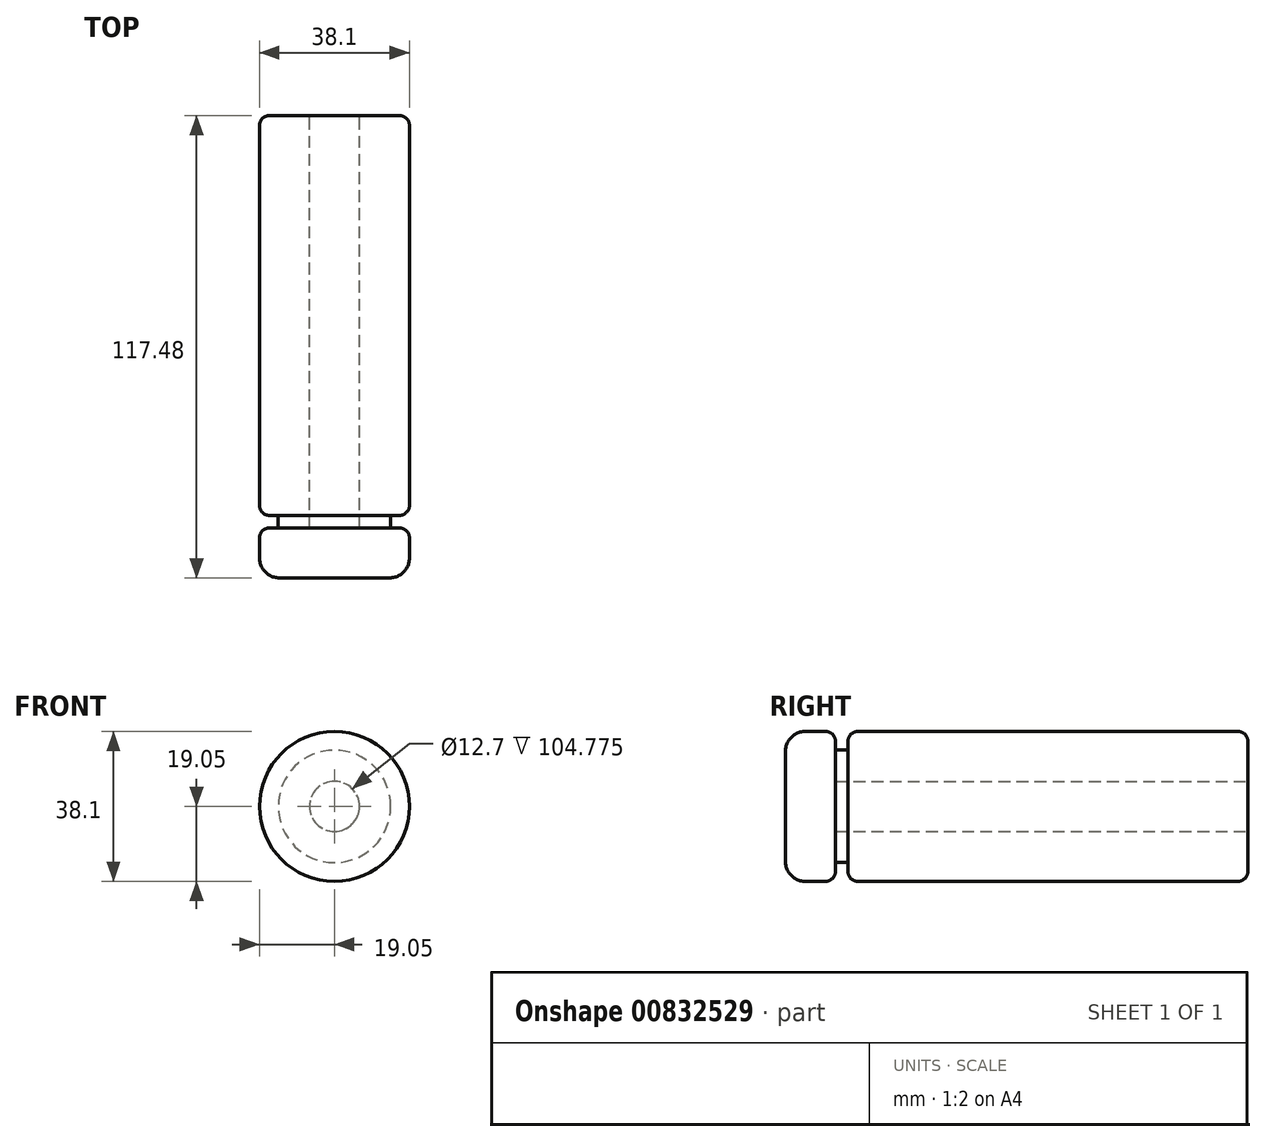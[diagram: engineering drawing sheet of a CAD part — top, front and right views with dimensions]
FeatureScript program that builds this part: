
annotation { "Feature Type Name" : "Feature", "Feature Type Description" : "" }
export const myFeature = defineFeature(function(context is Context, id is Id, definition is map)
    precondition{}
    {
        {
            var Q0;
            Q0=qCreatedBy(makeId("Front.planeOp"),FACE);
            var sketch = newSketch(context, id + "F0", { "sketchPlane" : qUnion([Q0])});
            skCircle(sketch, "E0", {"center": v(0, 0) * mm, "radius": 19.05 * mm});
            skSolve(sketch);
        }
        {
            var Q0;
            Q0=makeQuery(id+"F0.imprint","IMPRINT",FACE,{"disambiguationData":[TD([[makeQuery(id+"F0.imprint","IMPRINT",EDGE,{"derivedFrom":sQuery(id+"F0.wireOp",EDGE,"E0")}),1.0]])]});
            extrude(context, id + "F1", {"entities" : qUnion([Q0]), "depth" : 101.6 * mm, "offsetDistance" : 25.4 * mm});
        }
        {
            var Q0;
            Q0=makeQuery(id+"F1.opExtrude","CAP_EDGE",EDGE,{"disambiguationData":[OSD([sQuery(id+"F0.wireOp",EDGE,"E0")])],"isStart":false});
            var Q1;
            Q1=makeQuery(id+"F1.opExtrude","CAP_EDGE",EDGE,{"disambiguationData":[OSD([sQuery(id+"F0.wireOp",EDGE,"E0")])],"isStart":true});
            fillet(context, id + "F2", {"entities" : qUnion([Q0, Q1]), "radius" : 2.54 * mm, "tangentPropagation" : true, "allowEdgeOverflow" : false});
        }
        {
            var Q0;
            Q0=makeQuery(id+"F1.opExtrude","CAP_FACE",FACE,{"disambiguationData":[OSD([sQuery(id+"F0.wireOp",EDGE,"E0")])],"isStart":true});
            var sketch = newSketch(context, id + "F3", { "sketchPlane" : qUnion([Q0])});
            skCircle(sketch, "E1", {"center": v(0, 0) * mm, "radius": 6.35 * mm});
            skSolve(sketch);
        }
        {
            var Q0;
            Q0=makeQuery(id+"F1.opExtrude","CAP_FACE",FACE,{"disambiguationData":[OSD([sQuery(id+"F0.wireOp",EDGE,"E0")])],"isStart":false});
            var sketch = newSketch(context, id + "F4", { "sketchPlane" : qUnion([Q0])});
            skCircle(sketch, "E2", {"center": v(0, 0) * mm, "radius": 6.35 * mm});
            skSolve(sketch);
        }
        {
            var Q0;
            Q0=makeQuery(id+"F4.imprint","IMPRINT",FACE,{"disambiguationData":[TD([[makeQuery(id+"F4.imprint","IMPRINT",EDGE,{"derivedFrom":sQuery(id+"F4.wireOp",EDGE,"E2")}),1.0]])]});
            var sketch = newSketch(context, id + "F5", { "sketchPlane" : qUnion([Q0])});
            skCircle(sketch, "E3", {"center": v(0, 0) * mm, "radius": 6.35 * mm});
            skCircle(sketch, "E4", {"center": v(0, 0) * mm, "radius": 14.29 * mm});
            skSolve(sketch);
        }
        {
            var Q0;
            Q0=makeQuery(id+"F5.imprint","IMPRINT",FACE,{"disambiguationData":[TD([[makeQuery(id+"F5.imprint","IMPRINT",EDGE,{"derivedFrom":sQuery(id+"F5.wireOp",EDGE,"E3")}),-1.0]])]});
            extrude(context, id + "F6", {"entities" : qUnion([Q0]), "operationType" : NewBodyOperationType.ADD, "depth" : 3.17 * mm, "offsetDistance" : 25.4 * mm});
        }
        {
            var Q0;
            Q0=makeQuery(id+"F6.opExtrude","CAP_FACE",FACE,{"disambiguationData":[OSD([sQuery(id+"F5.wireOp",EDGE,"E3"),sQuery(id+"F5.wireOp",EDGE,"E4")])],"isStart":false});
            var sketch = newSketch(context, id + "F7", { "sketchPlane" : qUnion([Q0])});
            skCircle(sketch, "E5", {"center": v(0, 0) * mm, "radius": 19.05 * mm});
            skSolve(sketch);
        }
        {
            var Q0;
            Q0=makeQuery(id+"F7.imprint","IMPRINT",FACE,{"disambiguationData":[TD([[makeQuery(id+"F7.imprint","IMPRINT",EDGE,{"derivedFrom":sQuery(id+"F7.wireOp",EDGE,"E5")}),1.0]])]});
            var Q1;
            Q1=makeQuery(id+"F7.imprint","IMPRINT",FACE,{"disambiguationData":[TD([[makeQuery(id+"F7.imprint","IMPRINT",EDGE,{"derivedFrom":sQuery(id+"F7.wireOp",EDGE,"a4Jg7ElT-7Xqd-VF9B-7PKm-C04YS0PULk98")}),1.0]])]});
            extrude(context, id + "F8", {"entities" : qUnion([Q0, Q1]), "operationType" : NewBodyOperationType.ADD, "depth" : 25.4 * mm, "offsetDistance" : 25.4 * mm});
        }
        {
            var Q0;
            Q0=makeQuery(id+"F8.opExtrude","SWEPT_BODY",BODY,{"disambiguationData":[OSD([sQuery(id+"F5.wireOp",EDGE,"E4"),sQuery(id+"F7.wireOp",EDGE,"E5")])]});
            var Q1;
            Q1=makeQuery(id+"F8.opExtrude","SWEPT_BODY",BODY,{"disambiguationData":[OSD([sQuery(id+"F7.wireOp",EDGE,"a4Jg7ElT-7Xqd-VF9B-7PKm-C04YS0PULk98")])]});
            deleteBodies(context, id + "F9", {"entities" : qUnion([Q0, Q1])});
        }
        {
            var Q0;
            Q0=makeQuery(id+"F6.opExtrude","CAP_FACE",FACE,{"disambiguationData":[OSD([sQuery(id+"F5.wireOp",EDGE,"E3"),sQuery(id+"F5.wireOp",EDGE,"E4")])],"isStart":false});
            var sketch = newSketch(context, id + "F10", { "sketchPlane" : qUnion([Q0])});
            skCircle(sketch, "E6", {"center": v(0, 0) * mm, "radius": 19.05 * mm});
            skSolve(sketch);
        }
        {
            var Q0;
            Q0 = qSketchRegion(id + "F10", true);
            extrude(context, id + "F11", {"entities" : qUnion([Q0]), "operationType" : NewBodyOperationType.ADD, "depth" : 12.7 * mm, "offsetDistance" : 25.4 * mm});
        }
        {
            var Q0;
            Q0=makeQuery(id+"F11.opExtrude","CAP_EDGE",EDGE,{"disambiguationData":[OSD([sQuery(id+"F10.wireOp",EDGE,"E6")])],"isStart":true});
            fillet(context, id + "F12", {"entities" : qUnion([Q0]), "radius" : 2.54 * mm, "tangentPropagation" : true, "allowEdgeOverflow" : false});
        }
        {
            var Q0;
            Q0=makeQuery(id+"F11.opExtrude","CAP_EDGE",EDGE,{"disambiguationData":[OSD([sQuery(id+"F10.wireOp",EDGE,"E6")])],"isStart":false});
            fillet(context, id + "F13", {"entities" : qUnion([Q0]), "radius" : 5.08 * mm, "tangentPropagation" : true, "allowEdgeOverflow" : false});
        }
        {
            var Q0;
            Q0=makeQuery(id+"F3.imprint","IMPRINT",FACE,{"disambiguationData":[TD([[makeQuery(id+"F3.imprint","IMPRINT",EDGE,{"derivedFrom":sQuery(id+"F3.wireOp",EDGE,"E1")}),1.0]])]});
            var Q1;
            Q1=sQuery(id+"F3.wireOp",EDGE,"E1");
            var Q2;
            {var subQ0=sQuery(id+"F10.wireOp",EDGE,"E6");Q2=makeQuery(id+"F11.boolean.opBoolean","SPLIT",FACE,{"disambiguationData":[TD([makeQuery(id+"F6.opExtrude","SWEPT_FACE",FACE,{"disambiguationData":[OSD([sQuery(id+"F5.wireOp",EDGE,"E4")])]})])],"derivedFrom":makeQuery(id+"F11.opExtrude","CAP_FACE",FACE,{"disambiguationData":[OSD([subQ0])],"isStart":true})});}
            extrude(context, id + "F14", {"entities" : qUnion([Q0]), "operationType" : NewBodyOperationType.REMOVE, "surfaceEntities" : qUnion([Q1]), "endBound" : BoundingType.UP_TO_SURFACE, "oppositeDirection" : true, "depth" : 25.4 * mm, "endBoundEntityFace" : qUnion([Q2]), "offsetDistance" : 25.4 * mm});
        }
    });
